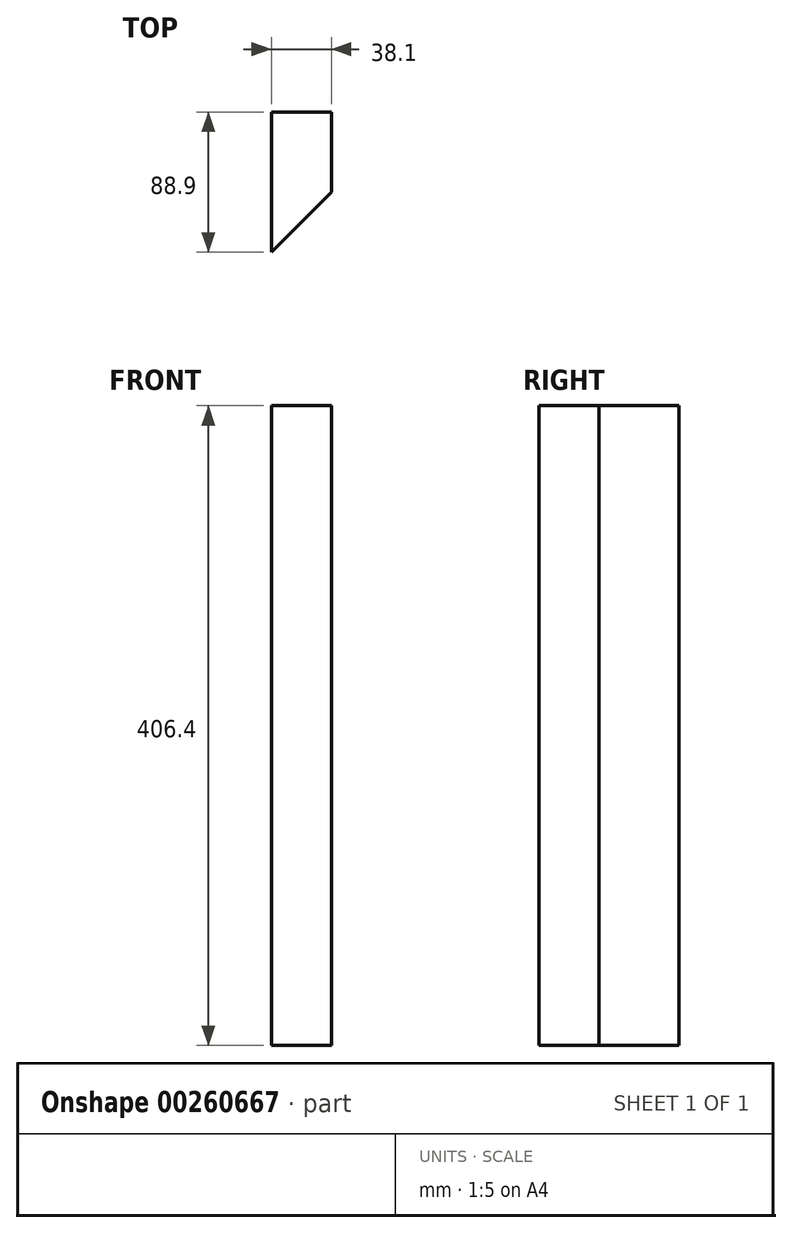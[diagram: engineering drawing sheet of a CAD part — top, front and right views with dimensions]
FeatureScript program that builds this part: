
annotation { "Feature Type Name" : "Feature", "Feature Type Description" : "" }
export const myFeature = defineFeature(function(context is Context, id is Id, definition is map)
    precondition{}
    {
        {
            var Q0;
            Q0=qCreatedBy(makeId("Top.planeOp"),FACE);
            var sketch = newSketch(context, id + "F0", { "sketchPlane" : qUnion([Q0])});
            skLineSegment(sketch, "E0", {"start": v(0, 0) * mm, "end": v(0, 88.9) * mm});
            skLineSegment(sketch, "E1", {"start": v(0, 88.9) * mm, "end": v(38.1, 88.9) * mm});
            skLineSegment(sketch, "E2", {"start": v(38.1, 88.9) * mm, "end": v(38.1, 38.1) * mm});
            skLineSegment(sketch, "E3", {"start": v(38.1, 38.1) * mm, "end": v(0, 0) * mm});
            skSolve(sketch);
        }
        {
            var Q0;
            Q0=makeQuery(id+"F0.imprint","IMPRINT",FACE,{"disambiguationData":[TD([[makeQuery(id+"F0.imprint","IMPRINT",EDGE,{"derivedFrom":sQuery(id+"F0.wireOp",EDGE,"E0")}),-1.0]])]});
            extrude(context, id + "F1", {"entities" : qUnion([Q0]), "depth" : 406.4 * mm});
        }
    });
